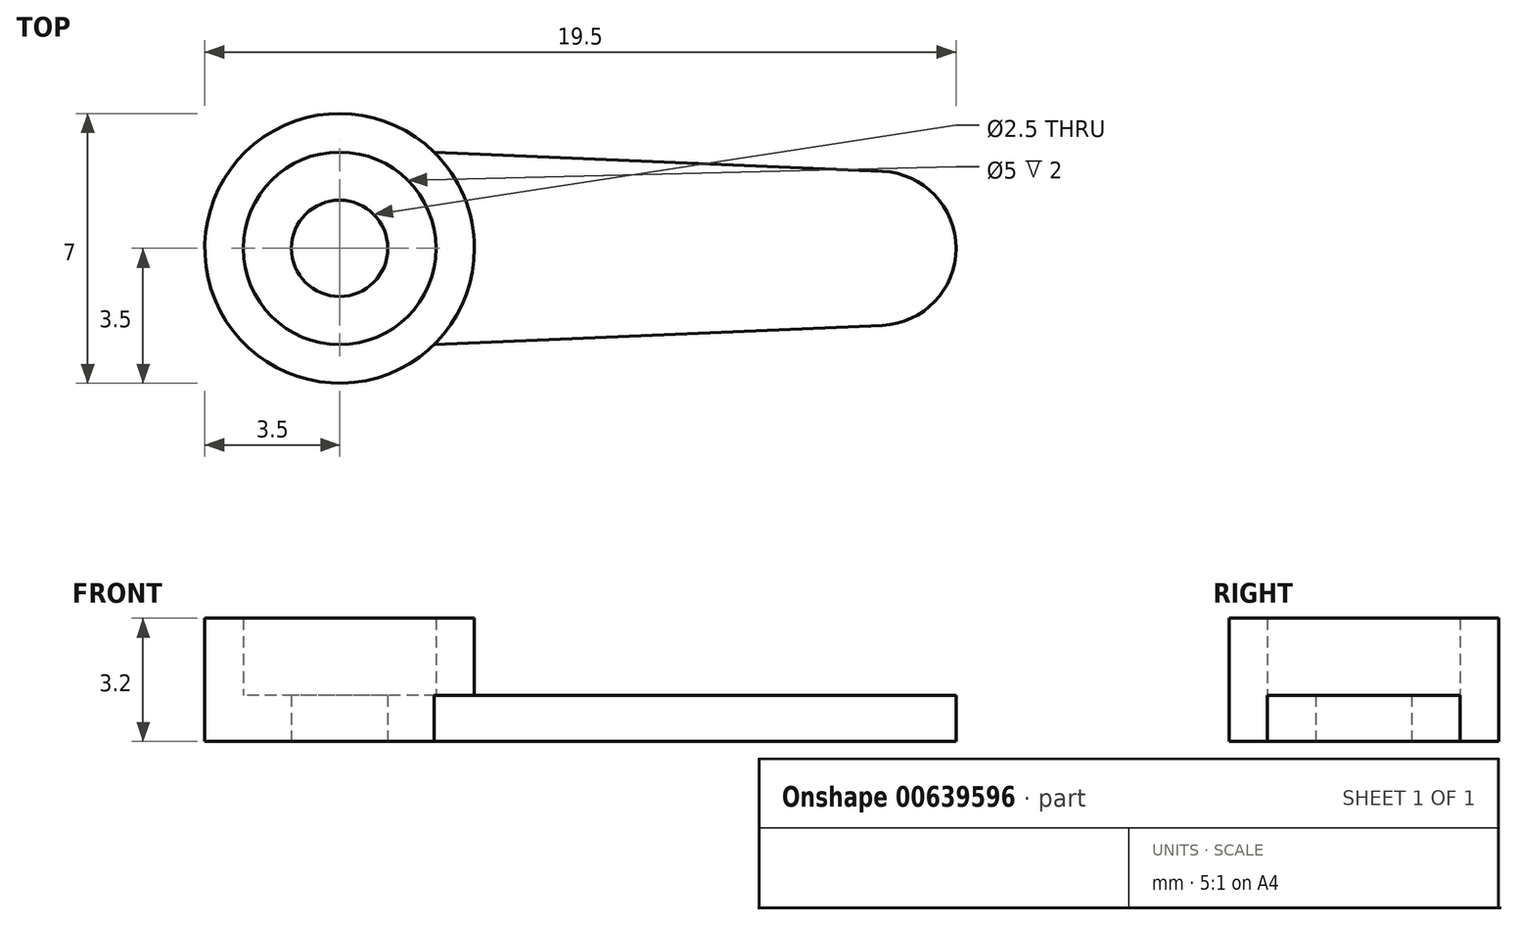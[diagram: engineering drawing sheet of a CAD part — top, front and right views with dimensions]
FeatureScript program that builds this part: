
annotation { "Feature Type Name" : "Feature", "Feature Type Description" : "" }
export const myFeature = defineFeature(function(context is Context, id is Id, definition is map)
    precondition{}
    {
        {
            var Q0;
            Q0=qCreatedBy(makeId("Top.planeOp"),FACE);
            var sketch = newSketch(context, id + "F0", { "sketchPlane" : qUnion([Q0])});
            skArc(sketch, "E0", {"start": v(2.45, 2.5) * mm, "mid": v(-3.5, 0) * mm, "end": v(2.45, -2.5) * mm});
            skArc(sketch, "E1", {"start": v(14.09, -2) * mm, "mid": v(16, 0) * mm, "end": v(14.09, 2) * mm});
            skLineSegment(sketch, "E2", {"start": v(2.45, 2.5) * mm, "end": v(14.09, 2) * mm});
            skLineSegment(sketch, "E3", {"start": v(2.45, -2.5) * mm, "end": v(14.09, -2) * mm});
            skCircle(sketch, "E4", {"center": v(0, 0) * mm, "radius": 1.25 * mm});
            skSolve(sketch);
        }
        {
            var Q0;
            Q0=makeQuery(id+"F0.imprint","IMPRINT",FACE,{"disambiguationData":[TD([[makeQuery(id+"F0.imprint","IMPRINT",EDGE,{"derivedFrom":sQuery(id+"F0.wireOp",EDGE,"E0")}),1.0]])]});
            extrude(context, id + "F1", {"entities" : qUnion([Q0]), "depth" : 1.2 * mm, "offsetDistance" : 25 * mm});
        }
        {
            var Q0;
            Q0=makeQuery(id+"F1.opExtrude","CAP_FACE",FACE,{"disambiguationData":[OSD([sQuery(id+"F0.wireOp",EDGE,"E0"),sQuery(id+"F0.wireOp",EDGE,"E1"),sQuery(id+"F0.wireOp",EDGE,"E2"),sQuery(id+"F0.wireOp",EDGE,"E3"),sQuery(id+"F0.wireOp",EDGE,"E4")])],"isStart":false});
            var sketch = newSketch(context, id + "F2", { "sketchPlane" : qUnion([Q0])});
            skCircle(sketch, "E5", {"center": v(0, 0) * mm, "radius": 2.5 * mm});
            skCircle(sketch, "E6", {"center": v(0, 0) * mm, "radius": 3.5 * mm});
            skSolve(sketch);
        }
        {
            var Q0;
            Q0=makeQuery(id+"F2.imprint","IMPRINT",FACE,{"disambiguationData":[TD([[makeQuery(id+"F2.imprint","IMPRINT",EDGE,{"derivedFrom":sQuery(id+"F2.wireOp",EDGE,"E5")}),-1.0]])]});
            extrude(context, id + "F3", {"entities" : qUnion([Q0]), "operationType" : NewBodyOperationType.ADD, "depth" : 2 * mm, "offsetDistance" : 25 * mm});
        }
    });
